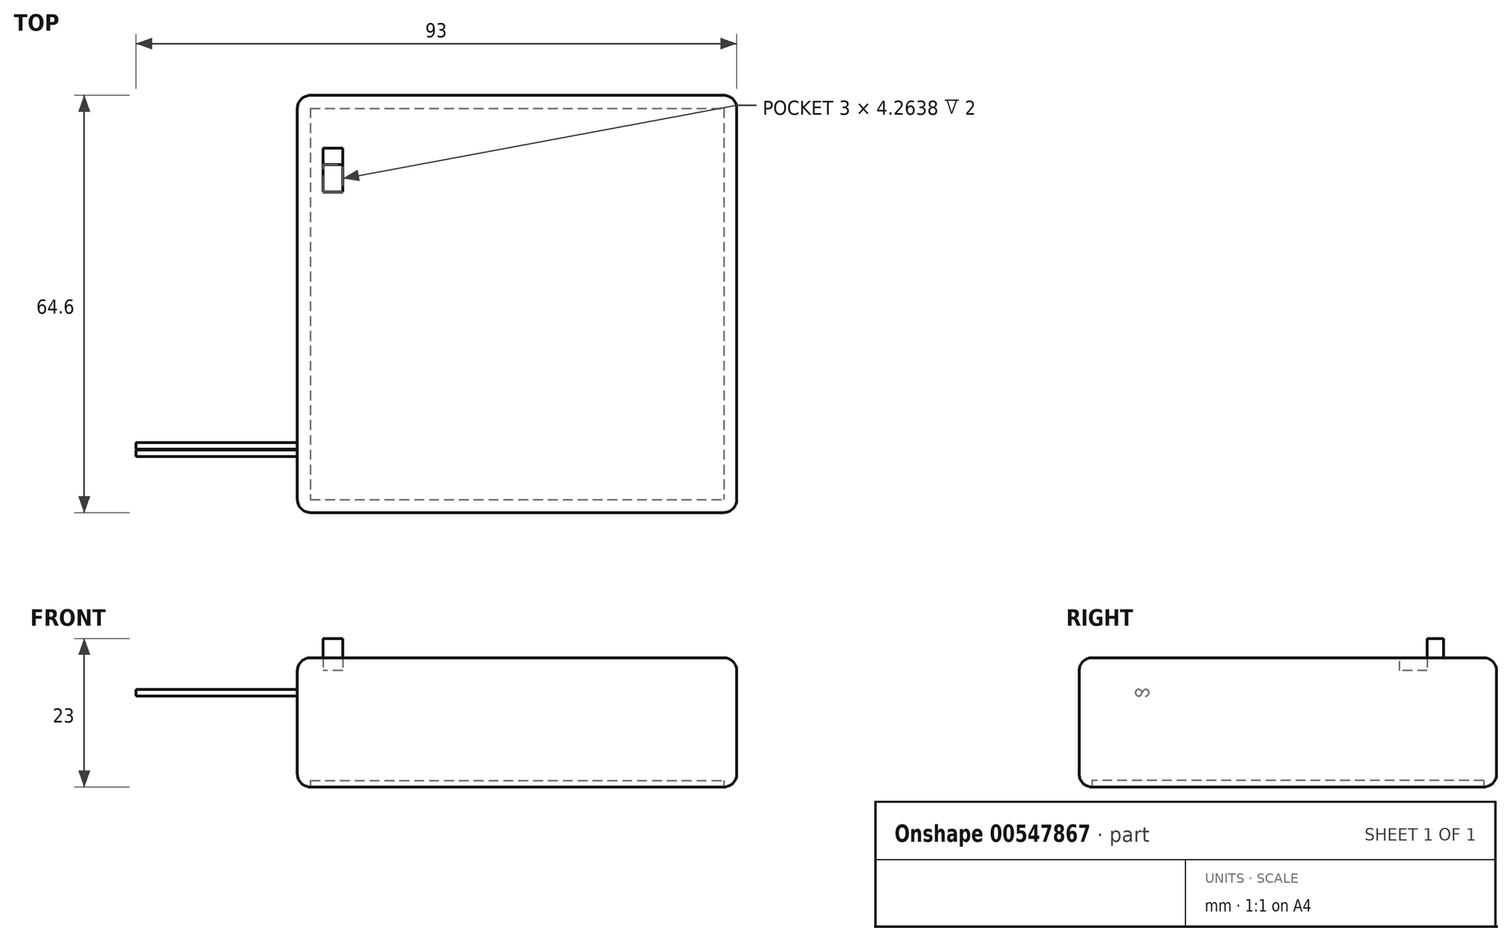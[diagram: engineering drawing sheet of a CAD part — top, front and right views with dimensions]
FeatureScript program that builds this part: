
annotation { "Feature Type Name" : "Feature", "Feature Type Description" : "" }
export const myFeature = defineFeature(function(context is Context, id is Id, definition is map)
    precondition{}
    {
        {
            var Q0;
            Q0=qCreatedBy(makeId("Top.planeOp"),FACE);
            var sketch = newSketch(context, id + "F0", { "sketchPlane" : qUnion([Q0])});
            skLineSegment(sketch, "E0.bottom", {"start": v(0, 0) * mm, "end": v(68, 0) * mm});
            skLineSegment(sketch, "E0.top", {"start": v(0, -64.6) * mm, "end": v(68, -64.6) * mm});
            skLineSegment(sketch, "E0.left", {"start": v(0, 0) * mm, "end": v(0, -64.6) * mm});
            skLineSegment(sketch, "E0.right", {"start": v(68, 0) * mm, "end": v(68, -64.6) * mm});
            skSolve(sketch);
        }
        {
            var Q0;
            Q0 = qSketchRegion(id + "F0", true);
            extrude(context, id + "F1", {"entities" : qUnion([Q0]), "depth" : 20 * mm, "offsetDistance" : 25 * mm});
        }
        {
            var Q0;
            Q0=makeQuery(id+"F1.opExtrude","CAP_FACE",FACE,{"disambiguationData":[OSD([sQuery(id+"F0.wireOp",EDGE,"E0.bottom"),sQuery(id+"F0.wireOp",EDGE,"E0.top"),sQuery(id+"F0.wireOp",EDGE,"E0.left"),sQuery(id+"F0.wireOp",EDGE,"E0.right")])],"isStart":false});
            var Q1;
            Q1=makeQuery(id+"F1.opExtrude","CAP_FACE",FACE,{"disambiguationData":[OSD([sQuery(id+"F0.wireOp",EDGE,"E0.bottom"),sQuery(id+"F0.wireOp",EDGE,"E0.top"),sQuery(id+"F0.wireOp",EDGE,"E0.left"),sQuery(id+"F0.wireOp",EDGE,"E0.right")])],"isStart":true});
            var Q2;
            Q2=makeQuery(id+"F1.opExtrude","SWEPT_EDGE",EDGE,{"disambiguationData":[OSD([sQuery(id+"F0.wireOp",EDGE,"E0.top"),sQuery(id+"F0.wireOp",EDGE,"E0.right")])]});
            var Q3;
            Q3=makeQuery(id+"F1.opExtrude","SWEPT_EDGE",EDGE,{"disambiguationData":[OSD([sQuery(id+"F0.wireOp",EDGE,"E0.bottom"),sQuery(id+"F0.wireOp",EDGE,"E0.right")])]});
            var Q4;
            Q4=makeQuery(id+"F1.opExtrude","SWEPT_EDGE",EDGE,{"disambiguationData":[OSD([sQuery(id+"F0.wireOp",EDGE,"E0.bottom"),sQuery(id+"F0.wireOp",EDGE,"E0.left")])]});
            var Q5;
            Q5=makeQuery(id+"F1.opExtrude","SWEPT_EDGE",EDGE,{"disambiguationData":[OSD([sQuery(id+"F0.wireOp",EDGE,"E0.top"),sQuery(id+"F0.wireOp",EDGE,"E0.left")])]});
            fillet(context, id + "F2", {"entities" : qUnion([Q0, Q1, Q2, Q3, Q4, Q5]), "radius" : 2 * mm, "tangentPropagation" : true, "allowEdgeOverflow" : false});
        }
        {
            var Q0;
            Q0=makeQuery(id+"F1.opExtrude","CAP_FACE",FACE,{"disambiguationData":[OSD([sQuery(id+"F0.wireOp",EDGE,"E0.bottom"),sQuery(id+"F0.wireOp",EDGE,"E0.top"),sQuery(id+"F0.wireOp",EDGE,"E0.left"),sQuery(id+"F0.wireOp",EDGE,"E0.right")])],"isStart":false});
            var sketch = newSketch(context, id + "F3", { "sketchPlane" : qUnion([Q0])});
            skLineSegment(sketch, "E1.bottom", {"start": v(7, -8.18) * mm, "end": v(4, -8.18) * mm});
            skLineSegment(sketch, "E1.top", {"start": v(7, -15) * mm, "end": v(4, -15) * mm});
            skLineSegment(sketch, "E1.left", {"start": v(7, -8.18) * mm, "end": v(7, -15) * mm});
            skLineSegment(sketch, "E1.right", {"start": v(4, -8.18) * mm, "end": v(4, -15) * mm});
            skSolve(sketch);
        }
        {
            var Q0;
            Q0=makeQuery(id+"F3.imprint","IMPRINT",FACE,{"disambiguationData":[TD([[makeQuery(id+"F3.imprint","IMPRINT",EDGE,{"derivedFrom":sQuery(id+"F3.wireOp",EDGE,"E1.bottom")}),1.0]])]});
            extrude(context, id + "F4", {"entities" : qUnion([Q0]), "operationType" : NewBodyOperationType.REMOVE, "oppositeDirection" : true, "depth" : 2 * mm, "offsetDistance" : 25 * mm});
        }
        {
            var Q0;
            Q0=makeQuery(id+"F4.boolean.opBoolean","COPY",FACE,{"derivedFrom":makeQuery(id+"F4.opExtrude","CAP_FACE",FACE,{"disambiguationData":[OSD([sQuery(id+"F3.wireOp",EDGE,"E1.bottom"),sQuery(id+"F3.wireOp",EDGE,"E1.top"),sQuery(id+"F3.wireOp",EDGE,"E1.left"),sQuery(id+"F3.wireOp",EDGE,"E1.right")])],"isStart":false})});
            var sketch = newSketch(context, id + "F5", { "sketchPlane" : qUnion([Q0])});
            skLineSegment(sketch, "E2.bottom", {"start": v(7, -8.18) * mm, "end": v(4, -8.18) * mm});
            skLineSegment(sketch, "E2.top", {"start": v(7, -10.74) * mm, "end": v(4, -10.74) * mm});
            skLineSegment(sketch, "E2.left", {"start": v(7, -8.18) * mm, "end": v(7, -10.74) * mm});
            skLineSegment(sketch, "E2.right", {"start": v(4, -8.18) * mm, "end": v(4, -10.74) * mm});
            skSolve(sketch);
        }
        {
            var Q0;
            Q0=makeQuery(id+"F5.imprint","IMPRINT",FACE,{"disambiguationData":[TD([[makeQuery(id+"F5.imprint","IMPRINT",EDGE,{"derivedFrom":sQuery(id+"F5.wireOp",EDGE,"E2.bottom")}),1.0]])]});
            extrude(context, id + "F6", {"entities" : qUnion([Q0]), "operationType" : NewBodyOperationType.ADD, "depth" : 5 * mm, "offsetDistance" : 25 * mm});
        }
        {
            var Q0;
            Q0=makeQuery(id+"F1.opExtrude","SWEPT_FACE",FACE,{"disambiguationData":[OSD([sQuery(id+"F0.wireOp",EDGE,"E0.left")])]});
            var sketch = newSketch(context, id + "F7", { "sketchPlane" : qUnion([Q0])});
            skCircle(sketch, "E3", {"center": v(54.3, 14.6) * mm, "radius": 0.5 * mm});
            skCircle(sketch, "E4", {"center": v(55.4, 14.6) * mm, "radius": 0.5 * mm});
            skLineSegment(sketch, "E5", {"start": v(54.3, 14.6) * mm, "end": v(55.4, 14.6) * mm, "construction": true});
            skSolve(sketch);
        }
        {
            var Q0;
            Q0=makeQuery(id+"F7.imprint","IMPRINT",FACE,{"disambiguationData":[TD([[makeQuery(id+"F7.imprint","IMPRINT",EDGE,{"derivedFrom":sQuery(id+"F7.wireOp",EDGE,"E3")}),1.0]])]});
            var Q1;
            Q1=makeQuery(id+"F7.imprint","IMPRINT",FACE,{"disambiguationData":[TD([[makeQuery(id+"F7.imprint","IMPRINT",EDGE,{"derivedFrom":sQuery(id+"F7.wireOp",EDGE,"E4")}),1.0]])]});
            extrude(context, id + "F8", {"entities" : qUnion([Q0, Q1]), "operationType" : NewBodyOperationType.ADD, "depth" : 25 * mm, "offsetDistance" : 25 * mm});
        }
        {
            var Q0;
            Q0=makeQuery(id+"F1.opExtrude","CAP_FACE",FACE,{"disambiguationData":[OSD([sQuery(id+"F0.wireOp",EDGE,"E0.bottom"),sQuery(id+"F0.wireOp",EDGE,"E0.top"),sQuery(id+"F0.wireOp",EDGE,"E0.left"),sQuery(id+"F0.wireOp",EDGE,"E0.right")])],"isStart":true});
            var sketch = newSketch(context, id + "F9", { "sketchPlane" : qUnion([Q0])});
            skCircle(sketch, "E6", {"center": v(6, 32.3) * mm, "radius": 2.5 * mm});
            skLineSegment(sketch, "E7", {"start": v(6, 32.3) * mm, "end": v(2, 32.3) * mm, "construction": true});
            skSolve(sketch);
        }
        {
            var Q0;
            Q0=makeQuery(id+"F9.imprint","IMPRINT",FACE,{"disambiguationData":[TD([[makeQuery(id+"F9.imprint","IMPRINT",EDGE,{"derivedFrom":sQuery(id+"F9.wireOp",EDGE,"E6")}),1.0]])]});
            var Q1;
            Q1=makeQuery(id+"F9.imprint","IMPRINT",FACE,{"disambiguationData":[TD([[makeQuery(id+"F9.imprint","IMPRINT",EDGE,{"derivedFrom":sQuery(id+"F9.wireOp",EDGE,"E6")}),-1.0]])]});
            extrude(context, id + "F10", {"entities" : qUnion([Q0, Q1]), "operationType" : NewBodyOperationType.REMOVE, "oppositeDirection" : true, "depth" : 1 * mm, "offsetDistance" : 25 * mm});
        }
    });
